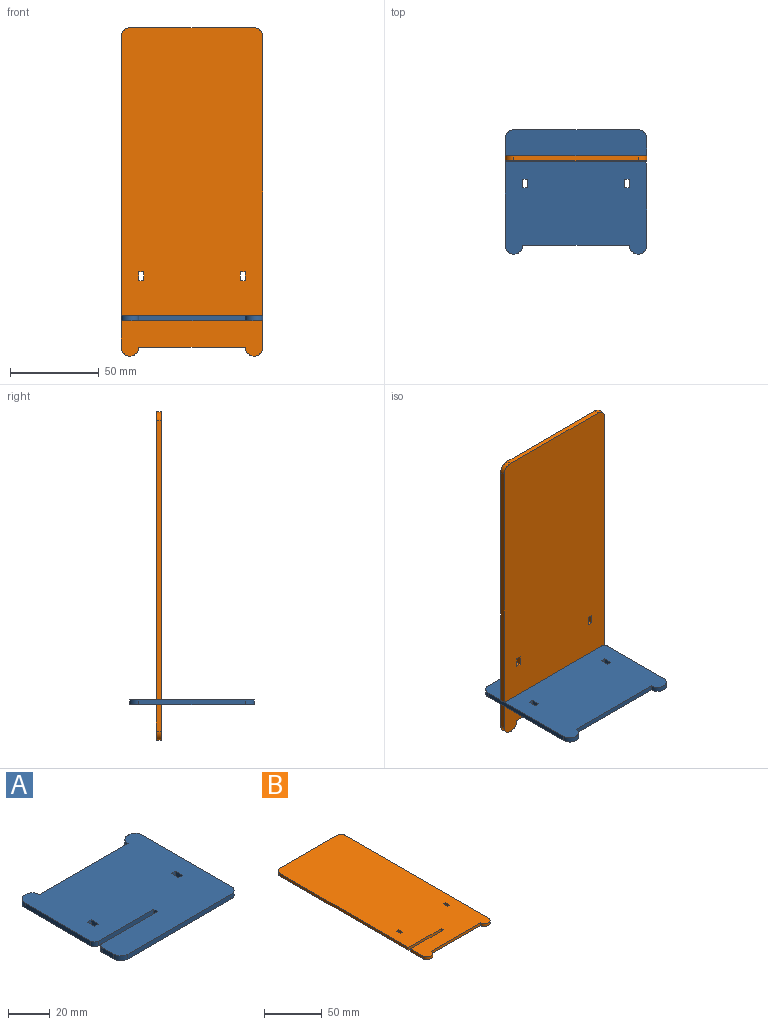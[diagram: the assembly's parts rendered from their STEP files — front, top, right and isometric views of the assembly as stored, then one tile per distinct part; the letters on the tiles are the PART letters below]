
ASSEMBLY  parts=2 mates=1
PART A: 24 faces, bbox 80x70x2.8 mm
  f0: plane 5x2.8mm, normal (1,0,0), area 14mm2, adj f1,f21,f22,f23
  f1: plane 2.8x2.7mm, normal (0,-1,0), area 7.6mm2, adj f0,f2,f22,f23
  f2: plane 5x2.8mm, normal (-1,0,0), area 14mm2, adj f1,f21,f22,f23
  f3: plane 2.8x2.7mm, normal (0,1,0), area 7.6mm2, adj f4,f19,f22,f23
  f4: plane 5x2.8mm, normal (1,0,0), area 14mm2, adj f3,f5,f22,f23
  f5: plane 2.8x2.7mm, normal (0,-1,0), area 7.6mm2, adj f4,f19,f22,f23
  f6: plane 2.8x2.7mm, normal (-1,0,0), area 7.6mm2, adj f7,f20,f22,f23
  f7: plane 37.5x2.8mm, normal (0,1,0), area 105mm2, adj f6,f8,f22,f23
  f8: cylinder r=2.5mm len=2.8mm, axis (0,0,-1), area 11mm2, adj f7,f9,f22,f23
  f9: plane 7.5x2.8mm, normal (-1,0,0), area 21mm2, adj f8,f10,f22,f23
  f10: cylinder r=5mm len=5mm, axis (0,0,-1), area 22mm2, adj f9,f11,f22,f23
  f11: plane 70x2.8mm, normal (0,-1,0), area 196mm2, adj f10,f12,f22,f23
  f12: cylinder r=5mm len=5mm, axis (0,0,-1), area 22mm2, adj f11,f13,f22,f23
  f13: plane 60x2.8mm, normal (1,0,0), area 168mm2, adj f12,f14,f22,f23
  f14: cylinder r=5mm len=10mm, axis (0,0,-1), area 44mm2, adj f13,f15,f22,f23
  f15: plane 60x2.8mm, normal (0,1,0), area 168mm2, adj f14,f16,f22,f23
  f16: cylinder r=5mm len=10mm, axis (0,0,-1), area 44mm2, adj f15,f17,f22,f23
  f17: plane 44.8x2.8mm, normal (-1,0,0), area 125.4mm2, adj f16,f18,f22,f23
  f18: cylinder r=2.5mm len=2.8mm, axis (0,0,-1), area 11mm2, adj f17,f20,f22,f23
  f19: plane 5x2.8mm, normal (-1,0,0), area 14mm2, adj f3,f5,f22,f23
  f20: plane 37.5x2.8mm, normal (0,-1,0), area 105mm2, adj f6,f18,f22,f23
  f21: plane 2.8x2.7mm, normal (0,1,0), area 7.6mm2, adj f0,f2,f22,f23
  f22: plane 80x70mm, normal (0,0,1), area 5130.1mm2, adj f0,f1,f2,f3,f4,f5,f6,f7
  f23: plane 80x70mm, normal (0,0,-1), area 5130.1mm2, adj f0,f1,f2,f3,f4,f5,f6,f7
PART B: 22 faces, bbox 80x185x2.8 mm
  f0: plane 2.8x2.7mm, normal (0,1,0), area 7.6mm2, adj f1,f19,f20,f21
  f1: plane 5x2.8mm, normal (1,0,0), area 14mm2, adj f0,f2,f20,f21
  f2: plane 2.8x2.7mm, normal (0,-1,0), area 7.6mm2, adj f1,f19,f20,f21
  f3: plane 2.8x2.7mm, normal (0,-1,0), area 7.6mm2, adj f4,f17,f20,f21
  f4: plane 5x2.8mm, normal (-1,0,0), area 14mm2, adj f3,f5,f20,f21
  f5: plane 2.8x2.7mm, normal (0,1,0), area 7.6mm2, adj f4,f17,f20,f21
  f6: plane 40x2.8mm, normal (0,-1,0), area 112mm2, adj f7,f18,f20,f21
  f7: plane 2.8x2.6mm, normal (-1,0,0), area 7.3mm2, adj f6,f8,f20,f21
  f8: plane 40x2.8mm, normal (0,1,0), area 112mm2, adj f7,f9,f20,f21
  f9: plane 15x2.8mm, normal (-1,0,0), area 42mm2, adj f8,f10,f20,f21
  f10: cylinder r=5mm len=10mm, axis (0,0,-1), area 44mm2, adj f9,f11,f20,f21
  f11: plane 60x2.8mm, normal (0,-1,0), area 168mm2, adj f10,f12,f20,f21
  f12: cylinder r=5mm len=10mm, axis (0,0,-1), area 44mm2, adj f11,f13,f20,f21
  f13: plane 175x2.8mm, normal (1,0,0), area 490mm2, adj f12,f14,f20,f21
  f14: cylinder r=5mm len=5mm, axis (0,0,-1), area 22mm2, adj f13,f15,f20,f21
  f15: plane 70x2.8mm, normal (0,1,0), area 196mm2, adj f14,f16,f20,f21
  f16: cylinder r=5mm len=5mm, axis (0,0,-1), area 22mm2, adj f15,f18,f20,f21
  f17: plane 5x2.8mm, normal (1,0,0), area 14mm2, adj f3,f5,f20,f21
  f18: plane 157.4x2.8mm, normal (-1,0,0), area 440.7mm2, adj f6,f16,f20,f21
  f19: plane 5x2.8mm, normal (-1,0,0), area 14mm2, adj f0,f2,f20,f21
  f20: plane 185x80mm, normal (0,0,1), area 14336.8mm2, adj f0,f1,f2,f3,f4,f5,f6,f7
  f21: plane 185x80mm, normal (0,0,-1), area 14336.8mm2, adj f0,f1,f2,f3,f4,f5,f6,f7
PLACE A rot(axis=(0,0,-1),180deg) t=(11.88,94.73,24.61)mm
PLACE B rot(axis=(1,0,0),90deg) t=(68.79,48.47,-45.87)mm
MATE fastened B.f7 <-> A.f6  axis (-1,0,0) through (-10.72,47.07,26.01)mm
